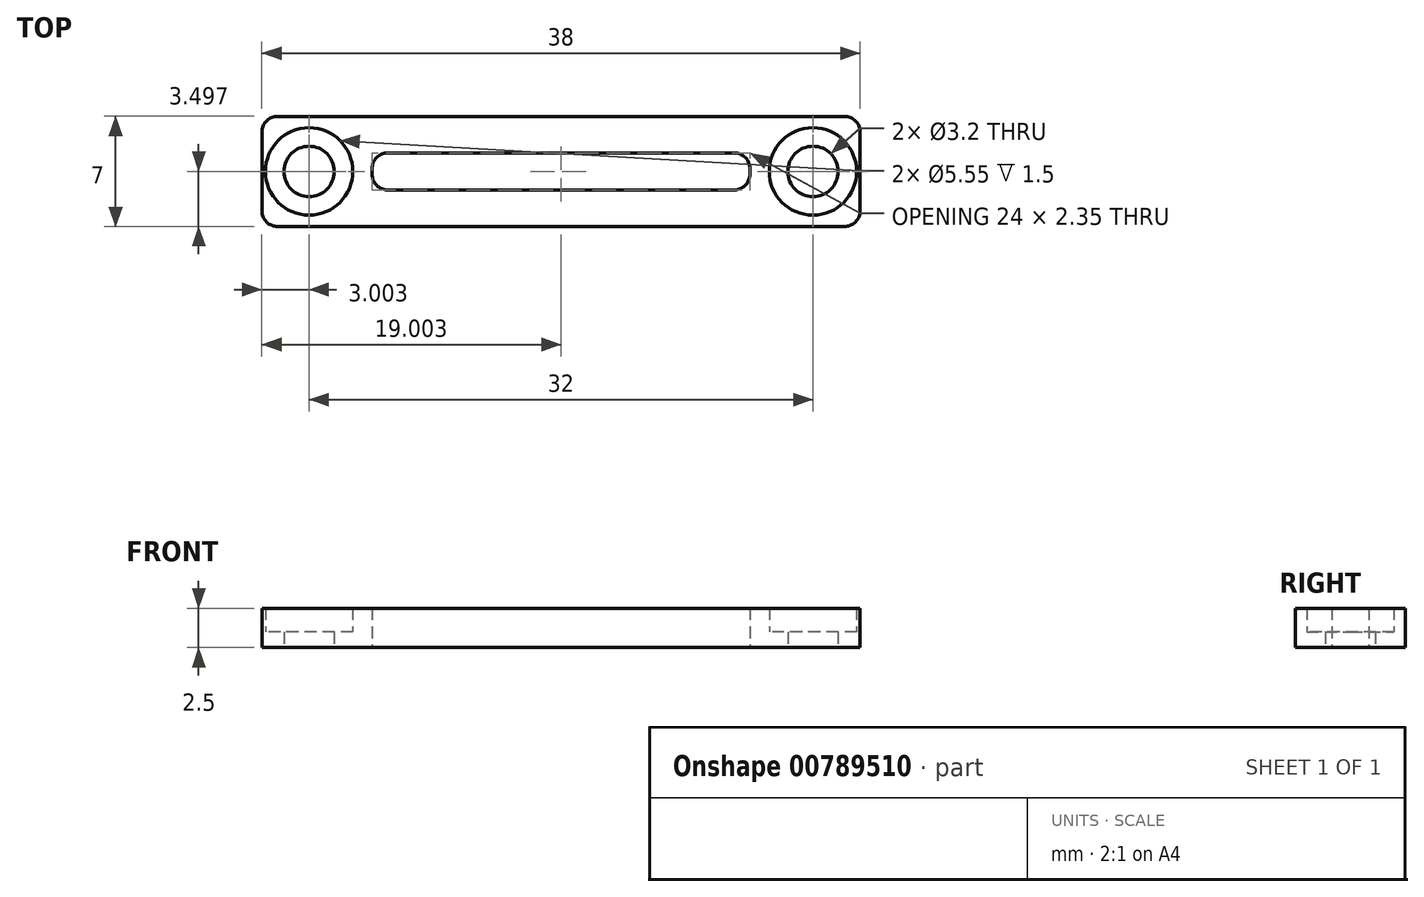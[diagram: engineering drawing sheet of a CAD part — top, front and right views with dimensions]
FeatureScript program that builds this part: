
annotation { "Feature Type Name" : "Feature", "Feature Type Description" : "" }
export const myFeature = defineFeature(function(context is Context, id is Id, definition is map)
    precondition{}
    {
        {
            var Q0;
            Q0=qCreatedBy(makeId("Top.planeOp"),FACE);
            var sketch = newSketch(context, id + "F0", { "sketchPlane" : qUnion([Q0])});
            skLineSegment(sketch, "E0.bottom", {"start": v(-19.83, 15.5) * mm, "end": v(16.17, 15.5) * mm});
            skLineSegment(sketch, "E0.top", {"start": v(-19.83, 8.5) * mm, "end": v(16.17, 8.5) * mm});
            skLineSegment(sketch, "E0.left", {"start": v(-20.83, 14.5) * mm, "end": v(-20.83, 9.5) * mm});
            skLineSegment(sketch, "E0.right", {"start": v(17.17, 14.5) * mm, "end": v(17.17, 9.5) * mm});
            skCircle(sketch, "E1", {"center": v(-17.83, 12) * mm, "radius": 1.6 * mm});
            skCircle(sketch, "E2", {"center": v(14.17, 12) * mm, "radius": 1.6 * mm});
            skLineSegment(sketch, "E3.bottom", {"start": v(-12.83, 13.17) * mm, "end": v(9.17, 13.17) * mm});
            skLineSegment(sketch, "E3.top", {"start": v(-12.83, 10.82) * mm, "end": v(9.17, 10.82) * mm});
            skLineSegment(sketch, "E3.left", {"start": v(-13.83, 12.17) * mm, "end": v(-13.83, 11.82) * mm});
            skLineSegment(sketch, "E3.right", {"start": v(10.17, 12.17) * mm, "end": v(10.17, 11.82) * mm});
            skPoint(sketch, "E4.visualSharp", {"position": v(-13.83, 13.17) * mm});
            skArc(sketch, "E4.filletArc", {"start": v(-12.83, 13.17) * mm, "mid": v(-13.53, 12.88) * mm, "end": v(-13.83, 12.17) * mm});
            skPoint(sketch, "E5.visualSharp", {"position": v(-13.83, 10.82) * mm});
            skArc(sketch, "E5.filletArc", {"start": v(-13.83, 11.82) * mm, "mid": v(-13.53, 11.11) * mm, "end": v(-12.83, 10.82) * mm});
            skPoint(sketch, "E6.visualSharp", {"position": v(10.17, 10.82) * mm});
            skArc(sketch, "E6.filletArc", {"start": v(9.17, 10.82) * mm, "mid": v(9.88, 11.11) * mm, "end": v(10.17, 11.82) * mm});
            skPoint(sketch, "E7.visualSharp", {"position": v(10.17, 13.17) * mm});
            skArc(sketch, "E7.filletArc", {"start": v(10.17, 12.17) * mm, "mid": v(9.88, 12.88) * mm, "end": v(9.17, 13.17) * mm});
            skPoint(sketch, "E8.visualSharp", {"position": v(-20.83, 15.5) * mm});
            skArc(sketch, "E8.filletArc", {"start": v(-19.83, 15.5) * mm, "mid": v(-20.53, 15.2) * mm, "end": v(-20.83, 14.5) * mm});
            skPoint(sketch, "E9.visualSharp", {"position": v(-20.83, 8.5) * mm});
            skArc(sketch, "E9.filletArc", {"start": v(-20.83, 9.5) * mm, "mid": v(-20.53, 8.79) * mm, "end": v(-19.83, 8.5) * mm});
            skPoint(sketch, "E10.visualSharp", {"position": v(17.17, 8.5) * mm});
            skArc(sketch, "E10.filletArc", {"start": v(16.17, 8.5) * mm, "mid": v(16.88, 8.79) * mm, "end": v(17.17, 9.5) * mm});
            skPoint(sketch, "E11.visualSharp", {"position": v(17.17, 15.5) * mm});
            skArc(sketch, "E11.filletArc", {"start": v(17.17, 14.5) * mm, "mid": v(16.88, 15.2) * mm, "end": v(16.17, 15.5) * mm});
            skCircle(sketch, "E12", {"center": v(-17.83, 12) * mm, "radius": 2.77 * mm});
            skCircle(sketch, "E13", {"center": v(14.17, 12) * mm, "radius": 2.77 * mm});
            skSolve(sketch);
        }
        {
            var Q0;
            Q0=makeQuery(id+"F0.imprint","IMPRINT",FACE,{"disambiguationData":[TD([[makeQuery(id+"F0.imprint","IMPRINT",EDGE,{"derivedFrom":sQuery(id+"F0.wireOp",EDGE,"E0.bottom")}),-1.0]])]});
            var Q1;
            Q1=makeQuery(id+"F0.imprint","IMPRINT",FACE,{"disambiguationData":[TD([[makeQuery(id+"F0.imprint","IMPRINT",EDGE,{"derivedFrom":sQuery(id+"F0.wireOp",EDGE,"E1")}),-1.0]])]});
            var Q2;
            Q2=makeQuery(id+"F0.imprint","IMPRINT",FACE,{"disambiguationData":[TD([[makeQuery(id+"F0.imprint","IMPRINT",EDGE,{"derivedFrom":sQuery(id+"F0.wireOp",EDGE,"E2")}),-1.0]])]});
            extrude(context, id + "F1", {"entities" : qUnion([Q0, Q1, Q2]), "depth" : 1 * mm, "offsetDistance" : 25 * mm});
        }
        {
            var Q0;
            Q0=makeQuery(id+"F0.imprint","IMPRINT",FACE,{"disambiguationData":[TD([[makeQuery(id+"F0.imprint","IMPRINT",EDGE,{"derivedFrom":sQuery(id+"F0.wireOp",EDGE,"E0.bottom")}),-1.0]])]});
            extrude(context, id + "F2", {"entities" : qUnion([Q0]), "operationType" : NewBodyOperationType.ADD, "depth" : 2.5 * mm, "offsetDistance" : 25 * mm});
        }
    });
